# Revit family: Door_Lift_UltiGroup_Fold-Plus
name_source: partatom
category: Doors
revit_build: Autodesk Revit 2018 (Build: 20170223_1515(x64)
units: mm (PartAtom-declared; Revit-internal decimal feet)

## family parameters
Always vertical = Yes
Cut with Voids When Loaded = No
Host = Wall
OmniClass Number = 23.30.10.17.17
OmniClass Title = Folding Doors and Grilles
Room Calculation Point = No
Shared = No

## types (1)
- Type 1
    Analytic Construction = <None>
    Control box distance = 150 mm  [stored 0.492126 ft]
    Control box height = 1400 mm  [stored 4.59318 ft]
    Curtain length = 6200 mm  [stored 20.3412 ft]
    Description = Ulti Fold Door with Single front motor
    Door bottom safety edge = Ulti_Group_Fold_Single_Bottom_Edge
    Door frame depth = 350 mm  [stored 1.14829 ft]
    Door frame width = 150 mm  [stored 0.492126 ft]
    DoorFrameFinish_ANZRS = Galvanised Steel Finish or Painted with RAL colour options
    DoorFrameMaterial_ANZRS = Ulti_Group_Fold_Single_Frame
    DoorFrameType_ANZRS = Galvanised Steel Frame
    DoorGlazingHeight_ANZRS = 0 mm  [stored 0 ft]
    DoorGlazingWidth_ANZRS = 0 mm  [stored 0 ft]
    DoorGrilleHeight_ANZRS = 0 mm  [stored 0 ft]
    DoorGrilleWidth_ANZRS = 0 mm  [stored 0 ft]
    DoorGrille_ANZRS = Yes
    DoorNumberOfPanels_ANZRS = 0
    DoorPanelBWidth_ANZRS = 0 mm  [stored 0 ft]
    DoorPanelDepth_ANZRS = 0 mm  [stored 0 ft]
    DoorPanelFinish_ANZRS = PVC Fabric with RAL colour options
    DoorPanelHeight_ANZRS = 0 mm  [stored 0 ft]
    DoorPanelMaterial_ANZRS = Ulti_Group_Fold_Single_Panel_Material
    DoorPanelWidth_ANZRS = 0 mm  [stored 0 ft]
    Fax = 07 846 2467
    Function = Interior
    Headroom height = 1100 mm
    Height = 5000 mm  [stored 16.4042 ft]
    Hood depth = 350 mm  [stored 1.14829 ft]
    Hood height = 250 mm  [stored 0.82021 ft]
    InstallationGroup_ANZRS = 0
    Lifting straps material = Ulti_Group_Fold_Single_Lifting_Straps
    Manufacturer = Ulti Group Ltd.
    Model = Ulti Fold Plus
    ModifiedIssue_ANZRS = 0 $
    Motor depth = 385 mm  [stored 1.26312 ft]
    Motor height = 700 mm  [stored 2.29659 ft]
    Motor width = 290 mm  [stored 0.951444 ft]
    Number of wind load bars = 14
    Rough Height = 4000 mm  [stored 13.1234 ft]
    Rough Width = 4000 mm  [stored 13.1234 ft]
    Safety edge bottom = 200 mm  [stored 0.656168 ft]
    Send Message = http://ultigroup.co.nz
    Thickness = 4000 mm  [stored 13.1234 ft]
    URL = www.ultigroup.co.nz
    Wall Closure = By host
    Width = 6000 mm  [stored 19.685 ft]

note: [stored X ft] marks values corroborated as IEEE doubles in the binary element streams (Revit-internal decimal feet)

## geometry (parser evidence)
native form markers: Blend x2, Sweep x6
no freeform markers — native parametric forms only
